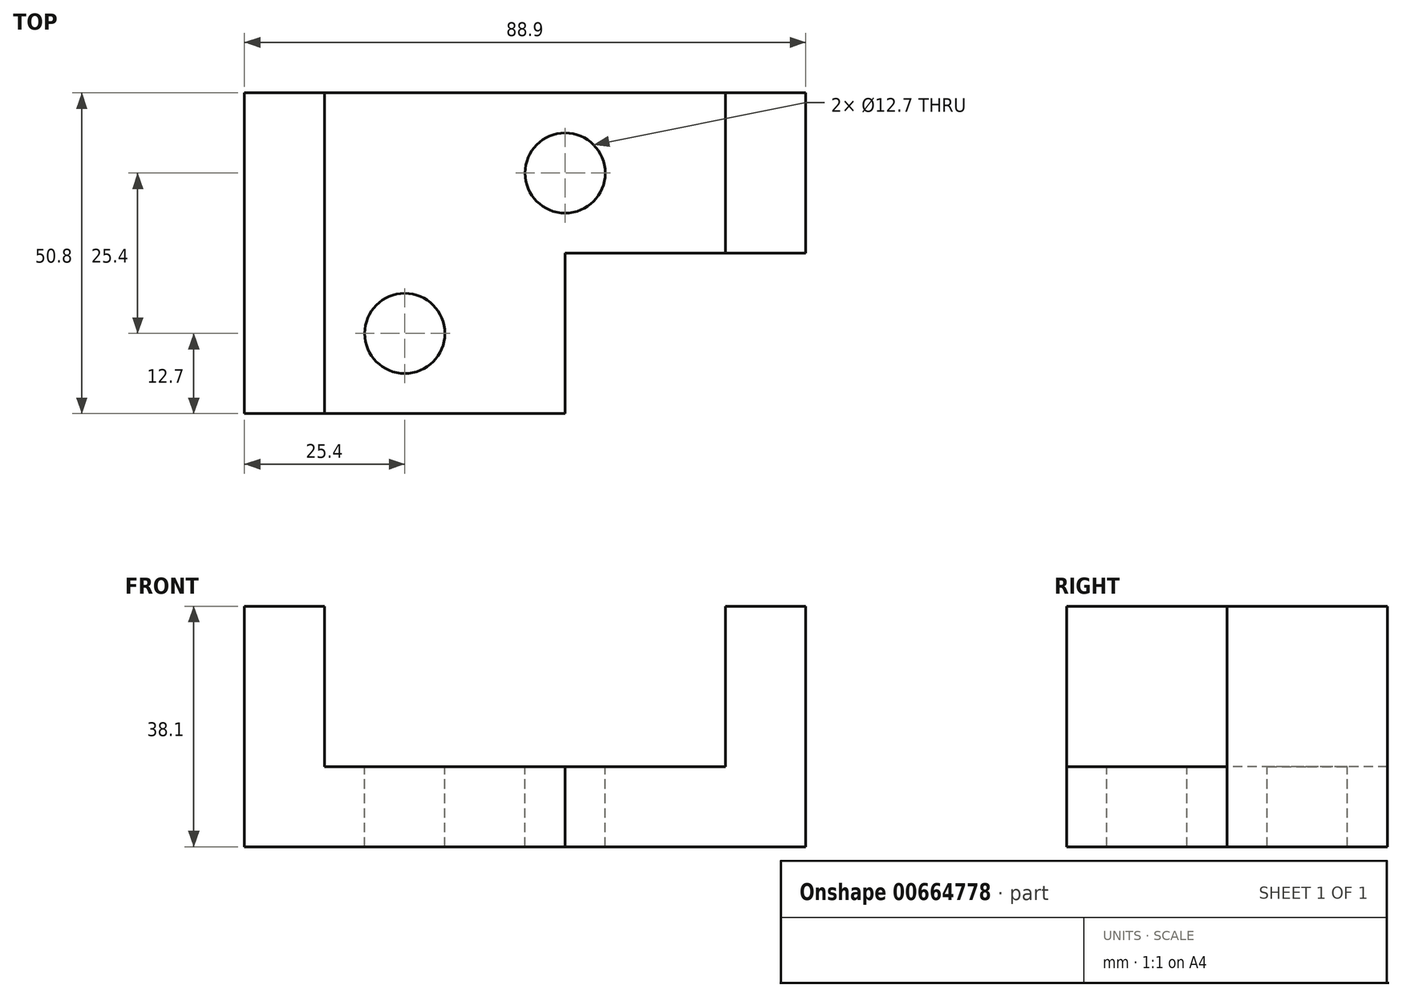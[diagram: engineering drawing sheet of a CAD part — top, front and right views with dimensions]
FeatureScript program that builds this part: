
annotation { "Feature Type Name" : "Feature", "Feature Type Description" : "" }
export const myFeature = defineFeature(function(context is Context, id is Id, definition is map)
    precondition{}
    {
        {
            var Q0;
            Q0=qCreatedBy(makeId("Front.planeOp"),FACE);
            var sketch = newSketch(context, id + "F0", { "sketchPlane" : qUnion([Q0])});
            skLineSegment(sketch, "E0.bottom", {"start": v(-44.45, 19.05) * mm, "end": v(44.45, 19.05) * mm});
            skLineSegment(sketch, "E0.top", {"start": v(-44.45, -19.05) * mm, "end": v(44.45, -19.05) * mm});
            skLineSegment(sketch, "E0.left", {"start": v(-44.45, 19.05) * mm, "end": v(-44.45, -19.05) * mm});
            skLineSegment(sketch, "E0.right", {"start": v(44.45, 19.05) * mm, "end": v(44.45, -19.05) * mm});
            skPoint(sketch, "E0.middle", {"position": v(0, 0) * mm});
            skSolve(sketch);
        }
        {
            var Q0;
            Q0 = qSketchRegion(id + "F0", true);
            extrude(context, id + "F1", {"entities" : qUnion([Q0]), "depth" : 50.8 * mm, "offsetDistance" : 25.4 * mm});
        }
        {
            var Q0;
            Q0=makeQuery(id+"F1.opExtrude","CAP_FACE",FACE,{"disambiguationData":[OSD([sQuery(id+"F0.wireOp",EDGE,"E0.bottom"),sQuery(id+"F0.wireOp",EDGE,"E0.top"),sQuery(id+"F0.wireOp",EDGE,"E0.left"),sQuery(id+"F0.wireOp",EDGE,"E0.right")])],"isStart":false});
            var sketch = newSketch(context, id + "F2", { "sketchPlane" : qUnion([Q0])});
            skLineSegment(sketch, "E1.bottom", {"start": v(-31.75, 19.05) * mm, "end": v(31.75, 19.05) * mm});
            skLineSegment(sketch, "E1.top", {"start": v(-31.75, -6.35) * mm, "end": v(31.75, -6.35) * mm});
            skLineSegment(sketch, "E1.left", {"start": v(-31.75, 19.05) * mm, "end": v(-31.75, -6.35) * mm});
            skLineSegment(sketch, "E1.right", {"start": v(31.75, 19.05) * mm, "end": v(31.75, -6.35) * mm});
            skSolve(sketch);
        }
        {
            var Q0;
            Q0=makeQuery(id+"F2.imprint","IMPRINT",FACE,{"disambiguationData":[TD([[makeQuery(id+"F2.imprint","IMPRINT",EDGE,{"derivedFrom":sQuery(id+"F2.wireOp",EDGE,"E1.bottom")}),-1.0]])]});
            extrude(context, id + "F3", {"entities" : qUnion([Q0]), "operationType" : NewBodyOperationType.REMOVE, "oppositeDirection" : true, "depth" : 50.8 * mm, "offsetDistance" : 25.4 * mm});
        }
        {
            var Q0;
            Q0=makeQuery(id+"F1.opExtrude","SWEPT_FACE",FACE,{"disambiguationData":[OSD([sQuery(id+"F0.wireOp",EDGE,"E0.right")])]});
            var sketch = newSketch(context, id + "F4", { "sketchPlane" : qUnion([Q0])});
            skLineSegment(sketch, "E2.bottom", {"start": v(-50.8, 19.05) * mm, "end": v(-25.4, 19.05) * mm});
            skLineSegment(sketch, "E2.top", {"start": v(-50.8, -19.05) * mm, "end": v(-25.4, -19.05) * mm});
            skLineSegment(sketch, "E2.left", {"start": v(-50.8, 19.05) * mm, "end": v(-50.8, -19.05) * mm});
            skLineSegment(sketch, "E2.right", {"start": v(-25.4, 19.05) * mm, "end": v(-25.4, -19.05) * mm});
            skSolve(sketch);
        }
        {
            var Q0;
            Q0=makeQuery(id+"F4.imprint","IMPRINT",FACE,{"disambiguationData":[TD([[makeQuery(id+"F4.imprint","IMPRINT",EDGE,{"derivedFrom":sQuery(id+"F4.wireOp",EDGE,"E2.bottom")}),-1.0]])]});
            extrude(context, id + "F5", {"entities" : qUnion([Q0]), "operationType" : NewBodyOperationType.REMOVE, "oppositeDirection" : true, "depth" : 38.1 * mm, "offsetDistance" : 25.4 * mm});
        }
        {
            var Q0;
            Q0=makeQuery(id+"F3.boolean.opBoolean","COPY",FACE,{"derivedFrom":makeQuery(id+"F3.opExtrude","SWEPT_FACE",FACE,{"disambiguationData":[OSD([sQuery(id+"F2.wireOp",EDGE,"E1.top")])]})});
            var sketch = newSketch(context, id + "F6", { "sketchPlane" : qUnion([Q0])});
            skCircle(sketch, "E3", {"center": v(-19.05, -38.1) * mm, "radius": 6.35 * mm});
            skPoint(sketch, "E3.first.point", {"position": v(-22.6, -32.83) * mm});
            skPoint(sketch, "E3.second.point", {"position": v(-13.63, -41.4) * mm});
            skPoint(sketch, "E3.third.point", {"position": v(-16.62, -32.23) * mm});
            skSolve(sketch);
        }
        {
            var Q0;
            Q0=makeQuery(id+"F6.imprint","IMPRINT",FACE,{"disambiguationData":[TD([[makeQuery(id+"F6.imprint","IMPRINT",EDGE,{"derivedFrom":sQuery(id+"F6.wireOp",EDGE,"E3")}),1.0]])]});
            extrude(context, id + "F7", {"entities" : qUnion([Q0]), "operationType" : NewBodyOperationType.REMOVE, "oppositeDirection" : true, "depth" : 12.7 * mm, "offsetDistance" : 25.4 * mm});
        }
        {
            var Q0;
            Q0=makeQuery(id+"F3.boolean.opBoolean","COPY",FACE,{"derivedFrom":makeQuery(id+"F3.opExtrude","SWEPT_FACE",FACE,{"disambiguationData":[OSD([sQuery(id+"F2.wireOp",EDGE,"E1.top")])]})});
            var sketch = newSketch(context, id + "F8", { "sketchPlane" : qUnion([Q0])});
            skCircle(sketch, "E4", {"center": v(6.35, -12.7) * mm, "radius": 6.35 * mm});
            skPoint(sketch, "E4.first.point", {"position": v(0.47, -10.3) * mm});
            skPoint(sketch, "E4.second.point", {"position": v(12.05, -15.5) * mm});
            skPoint(sketch, "E4.third.point", {"position": v(12.63, -11.74) * mm});
            skSolve(sketch);
        }
        {
            var Q0;
            Q0 = qSketchRegion(id + "F8", true);
            extrude(context, id + "F9", {"entities" : qUnion([Q0]), "operationType" : NewBodyOperationType.REMOVE, "oppositeDirection" : true, "depth" : 12.7 * mm, "offsetDistance" : 25.4 * mm});
        }
    });
